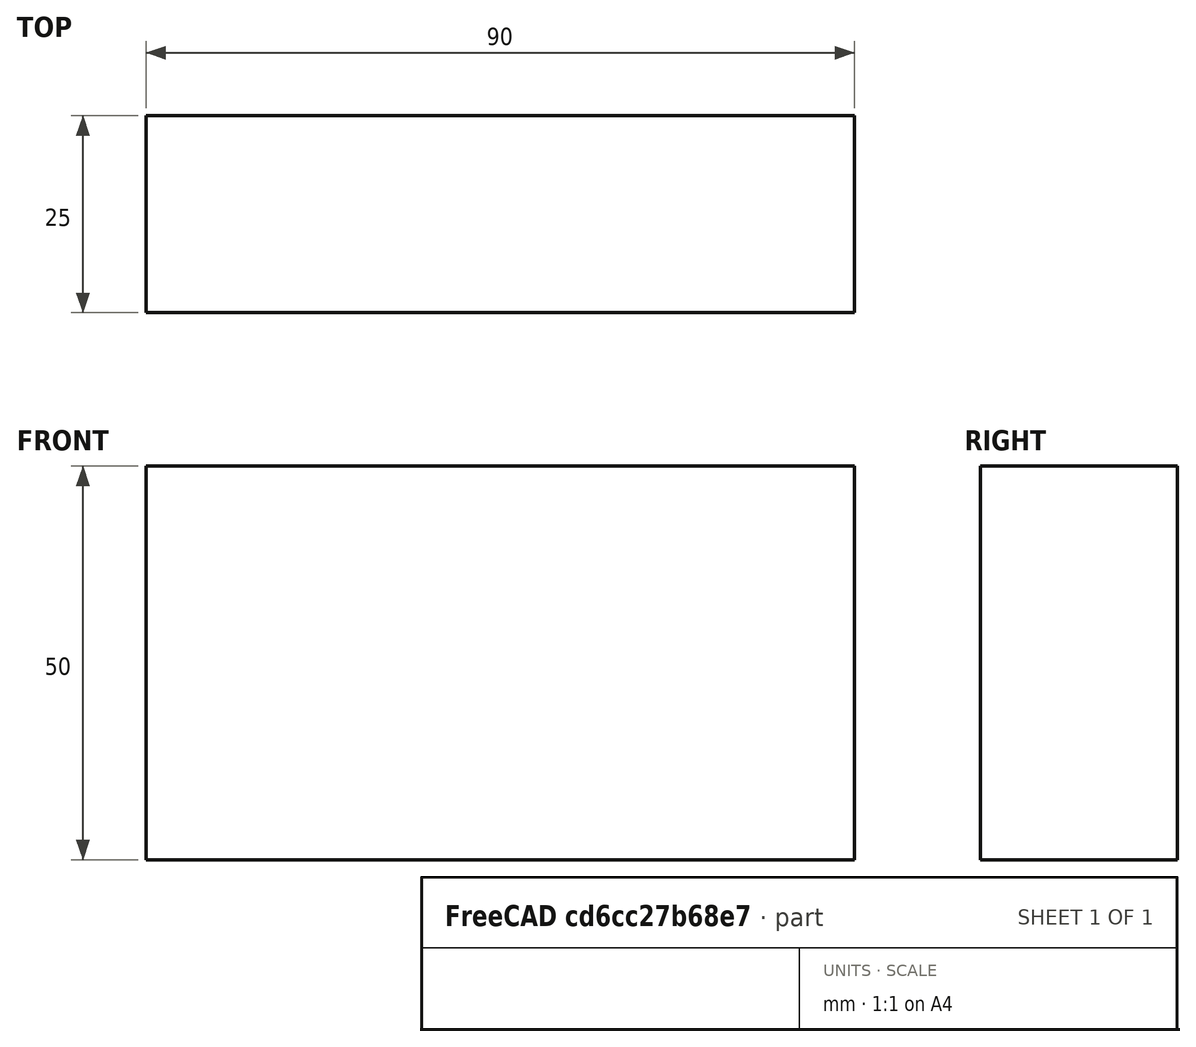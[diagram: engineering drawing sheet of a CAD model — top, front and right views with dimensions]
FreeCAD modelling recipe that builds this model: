
FCSTD DOCUMENT  (FreeCAD 0.15R4671 (Git))
Label: Flat Bar 90x25 EN10058 S235JR
License: All rights reserved
LicenseURL: http://en.wikipedia.org/wiki/All_rights_reserved
objects: Sketcher::SketchObject×1, Part::Extrusion×1
note: 2 computed .brp shape members not serialized (recipe doc carries the construction recipe); baked Part::Feature solids carry a one-line shape summary decoded from their .brp

FEATURE [Sketcher::SketchObject] Sketch
  sketch-geometry (4):
    g0: LineSegment StartX=-45 StartY=-12.5 StartZ=0 EndX=45 EndY=-12.5 EndZ=0
    g1: LineSegment StartX=45 StartY=-12.5 StartZ=0 EndX=45 EndY=12.5 EndZ=0
    g2: LineSegment StartX=45 StartY=12.5 StartZ=0 EndX=-45 EndY=12.5 EndZ=0
    g3: LineSegment StartX=-45 StartY=12.5 StartZ=0 EndX=-45 EndY=-12.5 EndZ=0
  constraints (12):
    c: Coincident(g0,g1)
    c: Coincident(g1,g2)
    c: Coincident(g2,g3)
    c: Coincident(g3,g0)
    c: Horizontal(g0)
    c: Horizontal(g2)
    c: Vertical(g1)
    c: Vertical(g3)
    c: Symmetric(g1,g2,g-2)
    c: Symmetric(g0,g1,g-1)
    c: DistanceY(g1) = 25
    c: DistanceX(g0) = 90
FEATURE [Part::Extrusion] Extrude  label="Flat Bar 90x25 EN10058 S235JR"
  Base = -> Sketch
  Dir = (0,0,50)
  Solid = true
